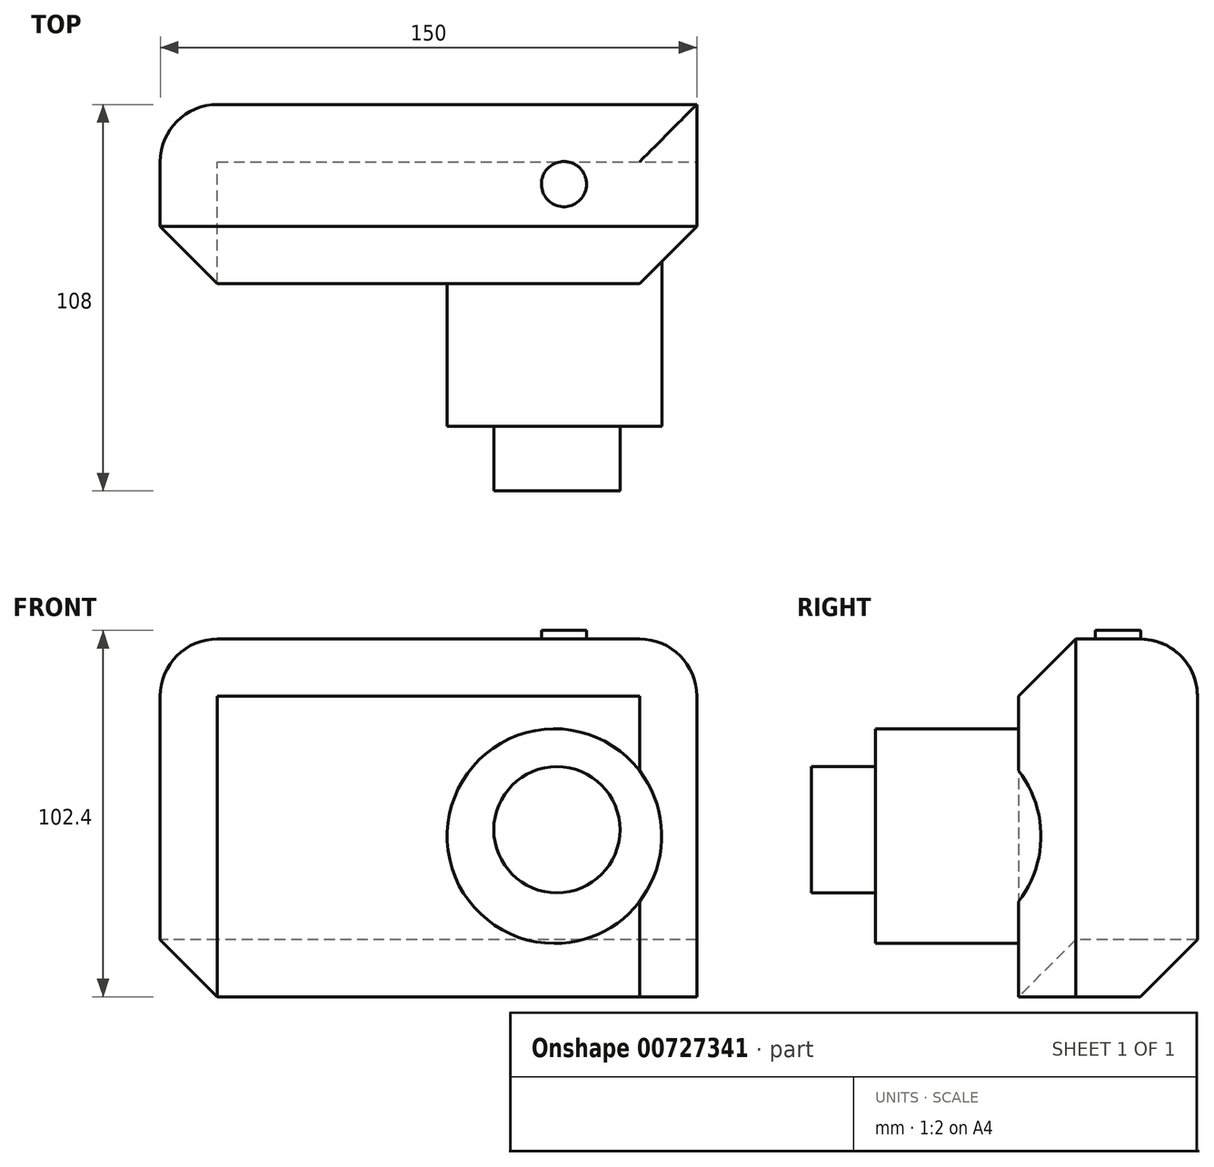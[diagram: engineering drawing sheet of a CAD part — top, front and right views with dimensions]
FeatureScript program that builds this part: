
annotation { "Feature Type Name" : "Feature", "Feature Type Description" : "" }
export const myFeature = defineFeature(function(context is Context, id is Id, definition is map)
    precondition{}
    {
        {
            var Q0;
            Q0=qCreatedBy(makeId("Top.planeOp"),FACE);
            var sketch = newSketch(context, id + "F0", { "sketchPlane" : qUnion([Q0])});
            skLineSegment(sketch, "E0.bottom", {"start": v(-165.56, -47.15) * mm, "end": v(-15.56, -47.15) * mm});
            skLineSegment(sketch, "E0.top", {"start": v(-165.56, -97.15) * mm, "end": v(-15.56, -97.15) * mm});
            skLineSegment(sketch, "E0.left", {"start": v(-165.56, -47.15) * mm, "end": v(-165.56, -97.15) * mm});
            skLineSegment(sketch, "E0.right", {"start": v(-15.56, -47.15) * mm, "end": v(-15.56, -97.15) * mm});
            skSolve(sketch);
        }
        {
            var Q0;
            Q0 = qSketchRegion(id + "F0", true);
            extrude(context, id + "F1", {"entities" : qUnion([Q0]), "depth" : 100 * mm, "offsetDistance" : 25 * mm});
        }
        {
            var Q0;
            Q0=makeQuery(id+"F1.opExtrude","SWEPT_FACE",FACE,{"disambiguationData":[OSD([sQuery(id+"F0.wireOp",EDGE,"E0.top")])]});
            var sketch = newSketch(context, id + "F2", { "sketchPlane" : qUnion([Q0])});
            skCircle(sketch, "E1", {"center": v(-55.34, 44.9) * mm, "radius": 30 * mm});
            skSolve(sketch);
        }
        {
            var Q0;
            Q0 = qSketchRegion(id + "F2", true);
            extrude(context, id + "F3", {"entities" : qUnion([Q0]), "operationType" : NewBodyOperationType.ADD, "depth" : 40 * mm, "offsetDistance" : 25 * mm});
        }
        {
            var Q0;
            Q0=makeQuery(id+"F1.opExtrude","CAP_EDGE",EDGE,{"disambiguationData":[OSD([sQuery(id+"F0.wireOp",EDGE,"E0.left")])],"isStart":false});
            fillet(context, id + "F4", {"entities" : qUnion([Q0]), "radius" : 16 * mm, "tangentPropagation" : true, "allowEdgeOverflow" : false});
        }
        {
            var Q0;
            Q0=makeQuery(id+"F1.opExtrude","CAP_EDGE",EDGE,{"disambiguationData":[OSD([sQuery(id+"F0.wireOp",EDGE,"E0.right")])],"isStart":false});
            var Q1;
            Q1=makeQuery(id+"F1.opExtrude","CAP_EDGE",EDGE,{"disambiguationData":[OSD([sQuery(id+"F0.wireOp",EDGE,"E0.bottom")])],"isStart":false});
            fillet(context, id + "F5", {"entities" : qUnion([Q0, Q1]), "radius" : 16 * mm, "tangentPropagation" : true, "allowEdgeOverflow" : false});
        }
        {
            var Q0;
            Q0=makeQuery(id+"F1.opExtrude","CAP_EDGE",EDGE,{"disambiguationData":[OSD([sQuery(id+"F0.wireOp",EDGE,"E0.left")])],"isStart":true});
            var Q1;
            {var subQ0=sQuery(id+"F0.wireOp",EDGE,"E0.left");Q1=makeQuery(id+"F5.opFillet","BLEND_EDGE",EDGE,{"blendedFrom":[makeQuery(id+"F1.opExtrude","SWEPT_EDGE",EDGE,{"disambiguationData":[OSD([sQuery(id+"F0.wireOp",EDGE,"E0.bottom"),subQ0])]}),makeQuery(id+"F1.opExtrude","SWEPT_FACE",FACE,{"disambiguationData":[OSD([subQ0])]})],"blendedInto":[makeQuery(id+"F1.opExtrude","SWEPT_FACE",FACE,{"disambiguationData":[OSD([subQ0])]})]});}
            var Q2;
            Q2=makeQuery(id+"F1.opExtrude","SWEPT_EDGE",EDGE,{"disambiguationData":[OSD([sQuery(id+"F0.wireOp",EDGE,"E0.top"),sQuery(id+"F0.wireOp",EDGE,"E0.left")])]});
            var Q3;
            {var subQ0=sQuery(id+"F0.wireOp",EDGE,"E0.left");var subQ1=sQuery(id+"F0.wireOp",EDGE,"E0.bottom");Q3=makeQuery(id+"F5.opFillet","BLEND_EDGE",EDGE,{"blendedFrom":[makeQuery(id+"F1.opExtrude","SWEPT_EDGE",EDGE,{"disambiguationData":[OSD([subQ1,subQ0])]}),makeQuery(id+"F1.opExtrude","CAP_FACE",FACE,{"disambiguationData":[OSD([subQ1,sQuery(id+"F0.wireOp",EDGE,"E0.top"),subQ0,sQuery(id+"F0.wireOp",EDGE,"E0.right")])],"isStart":true})],"blendedInto":[makeQuery(id+"F1.opExtrude","CAP_FACE",FACE,{"disambiguationData":[OSD([subQ1,sQuery(id+"F0.wireOp",EDGE,"E0.top"),subQ0,sQuery(id+"F0.wireOp",EDGE,"E0.right")])],"isStart":true})]});}
            chamfer(context, id + "F6", {"entities" : qUnion([Q0, Q1, Q2, Q3]), "width" : 16 * mm, "tangentPropagation" : true});
        }
        {
            var Q0;
            Q0=makeQuery(id+"F1.opExtrude","CAP_FACE",FACE,{"disambiguationData":[OSD([sQuery(id+"F0.wireOp",EDGE,"E0.bottom"),sQuery(id+"F0.wireOp",EDGE,"E0.top"),sQuery(id+"F0.wireOp",EDGE,"E0.left"),sQuery(id+"F0.wireOp",EDGE,"E0.right")])],"isStart":false});
            var sketch = newSketch(context, id + "F7", { "sketchPlane" : qUnion([Q0])});
            skCircle(sketch, "E2", {"center": v(-52.68, -69.4) * mm, "radius": 6.32 * mm});
            skSolve(sketch);
        }
        {
            var Q0;
            Q0 = qSketchRegion(id + "F7", true);
            extrude(context, id + "F8", {"entities" : qUnion([Q0]), "operationType" : NewBodyOperationType.ADD, "depth" : 2.4 * mm, "offsetDistance" : 25 * mm});
        }
        {
            var Q0;
            Q0=makeQuery(id+"F3.opExtrude","CAP_FACE",FACE,{"disambiguationData":[OSD([sQuery(id+"F2.wireOp",EDGE,"E1")])],"isStart":false});
            var sketch = newSketch(context, id + "F9", { "sketchPlane" : qUnion([Q0])});
            skCircle(sketch, "E3", {"center": v(-54.66, 46.7) * mm, "radius": 17.64 * mm});
            skSolve(sketch);
        }
        {
            var Q0;
            Q0 = qSketchRegion(id + "F9", true);
            extrude(context, id + "F10", {"entities" : qUnion([Q0]), "operationType" : NewBodyOperationType.ADD, "depth" : 18 * mm, "offsetDistance" : 25 * mm});
        }
    });
